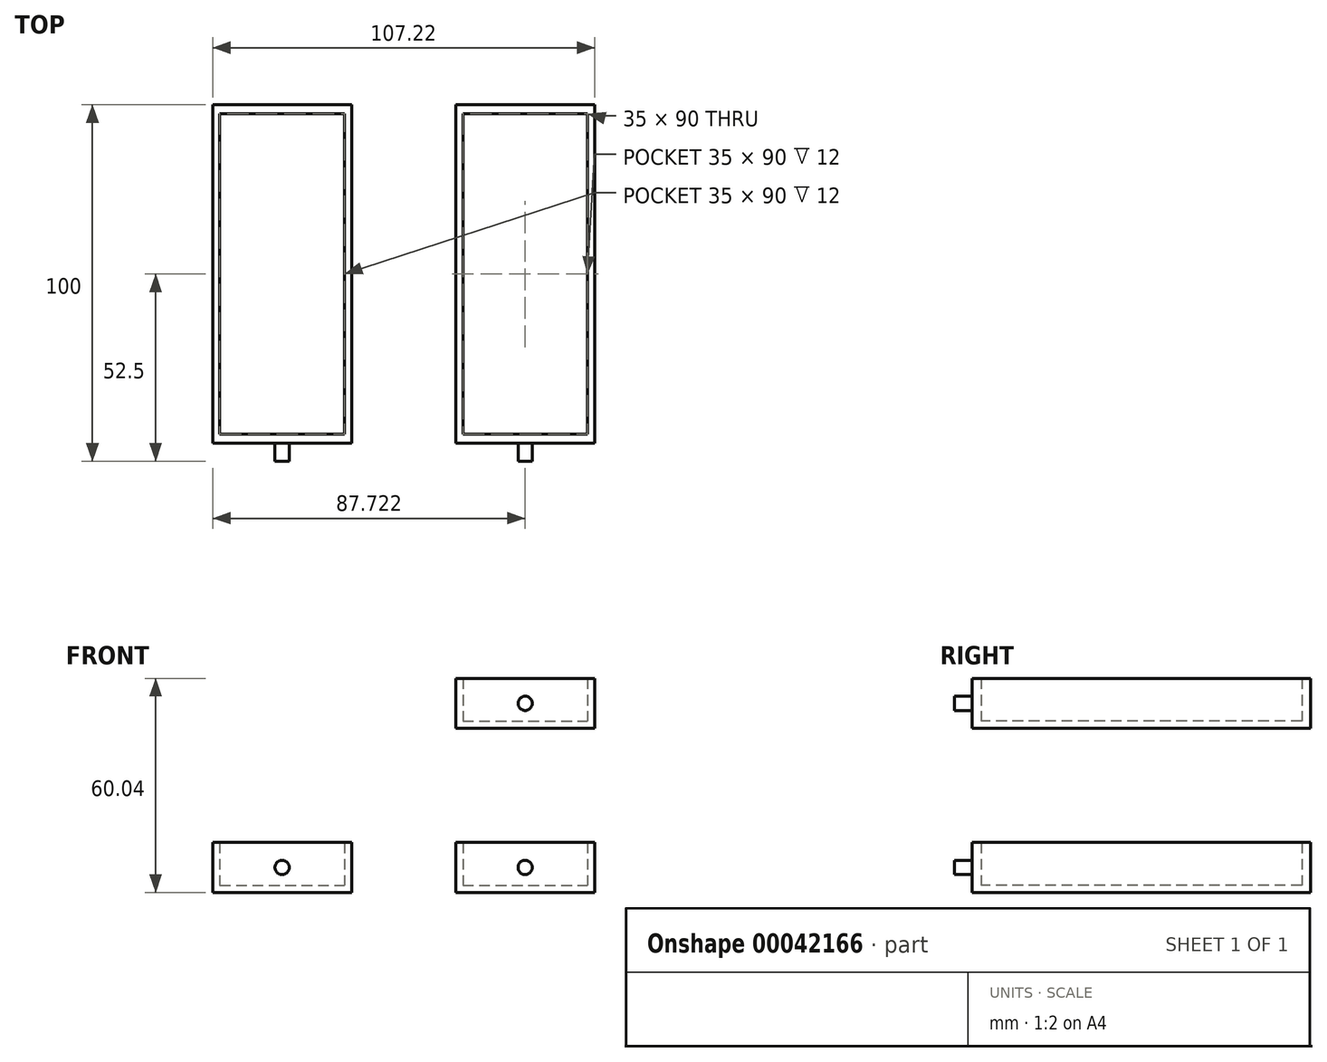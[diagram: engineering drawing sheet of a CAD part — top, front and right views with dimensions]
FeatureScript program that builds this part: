
annotation { "Feature Type Name" : "Feature", "Feature Type Description" : "" }
export const myFeature = defineFeature(function(context is Context, id is Id, definition is map)
    precondition{}
    {
        {
            var Q0;
            Q0=qCreatedBy(makeId("Top.planeOp"),FACE);
            var sketch = newSketch(context, id + "F0", { "sketchPlane" : qUnion([Q0])});
            skLineSegment(sketch, "E0.bottom", {"start": v(0, 0) * mm, "end": v(39, 0) * mm});
            skLineSegment(sketch, "E0.top", {"start": v(0, 95) * mm, "end": v(39, 95) * mm});
            skLineSegment(sketch, "E0.left", {"start": v(0, 0) * mm, "end": v(0, 95) * mm});
            skLineSegment(sketch, "E0.right", {"start": v(39, 0) * mm, "end": v(39, 95) * mm});
            skLineSegment(sketch, "E1.bottom", {"start": v(2, 92.5) * mm, "end": v(37, 92.5) * mm});
            skLineSegment(sketch, "E1.top", {"start": v(2, 2.5) * mm, "end": v(37, 2.5) * mm});
            skLineSegment(sketch, "E1.left", {"start": v(2, 92.5) * mm, "end": v(2, 2.5) * mm});
            skLineSegment(sketch, "E1.right", {"start": v(37, 92.5) * mm, "end": v(37, 2.5) * mm});
            skSolve(sketch);
        }
        {
            var Q0;
            Q0=makeQuery(id+"F0.imprint","IMPRINT",FACE,{"disambiguationData":[TD([[makeQuery(id+"F0.imprint","IMPRINT",EDGE,{"derivedFrom":sQuery(id+"F0.wireOp",EDGE,"E0.bottom")}),1.0]])]});
            extrude(context, id + "F1", {"entities" : qUnion([Q0]), "depth" : 14 * mm});
        }
        {
            var Q0;
            Q0=makeQuery(id+"F0.imprint","IMPRINT",FACE,{"disambiguationData":[TD([[makeQuery(id+"F0.imprint","IMPRINT",EDGE,{"derivedFrom":sQuery(id+"F0.wireOp",EDGE,"E1.bottom")}),-1.0]])]});
            extrude(context, id + "F2", {"entities" : qUnion([Q0]), "operationType" : NewBodyOperationType.ADD, "depth" : 2 * mm});
        }
        {
            var Q0;
            Q0=makeQuery(id+"F1.opExtrude","SWEPT_FACE",FACE,{"disambiguationData":[OSD([sQuery(id+"F0.wireOp",EDGE,"E0.bottom")])]});
            var sketch = newSketch(context, id + "F3", { "sketchPlane" : qUnion([Q0])});
            skCircle(sketch, "E2", {"center": v(19.5, 7) * mm, "radius": 2 * mm});
            skPoint(sketch, "E2.centerSnap0", {"position": v(19.5, 14) * mm});
            skSolve(sketch);
        }
        {
            var Q0;
            Q0 = qSketchRegion(id + "F3", true);
            extrude(context, id + "F4", {"entities" : qUnion([Q0]), "operationType" : NewBodyOperationType.ADD, "depth" : 5 * mm});
        }
        {
            var Q0;
            Q0=makeQuery(id+"F1.opExtrude","SWEPT_BODY",BODY,{"disambiguationData":[OSD([sQuery(id+"F0.wireOp",EDGE,"E0.bottom"),sQuery(id+"F0.wireOp",EDGE,"E0.top"),sQuery(id+"F0.wireOp",EDGE,"E0.left"),sQuery(id+"F0.wireOp",EDGE,"E0.right"),sQuery(id+"F0.wireOp",EDGE,"E1.bottom"),sQuery(id+"F0.wireOp",EDGE,"E1.top"),sQuery(id+"F0.wireOp",EDGE,"E1.left"),sQuery(id+"F0.wireOp",EDGE,"E1.right")])]});
            transform(context, id + "F5", {"entities" : qUnion([Q0]), "transformType" : TransformType.TRANSLATION_3D, "dx" : 68.22 * mm, "dy" : 0 * mm, "dz" : 0 * mm, "makeCopy" : true});
        }
        {
            var Q0;
            Q0=makeQuery(id+"F5.opPattern","COPY",BODY,{"derivedFrom":makeQuery(id+"F1.opExtrude","SWEPT_BODY",BODY,{"disambiguationData":[OSD([sQuery(id+"F0.wireOp",EDGE,"E0.bottom"),sQuery(id+"F0.wireOp",EDGE,"E0.top"),sQuery(id+"F0.wireOp",EDGE,"E0.left"),sQuery(id+"F0.wireOp",EDGE,"E0.right"),sQuery(id+"F0.wireOp",EDGE,"E1.bottom"),sQuery(id+"F0.wireOp",EDGE,"E1.top"),sQuery(id+"F0.wireOp",EDGE,"E1.left"),sQuery(id+"F0.wireOp",EDGE,"E1.right")])]}),"instanceName":"1"});
            transform(context, id + "F6", {"entities" : qUnion([Q0]), "transformType" : TransformType.TRANSLATION_3D, "dx" : 0 * mm, "dy" : 0 * mm, "dz" : 46.04 * mm, "makeCopy" : true});
        }
    });
